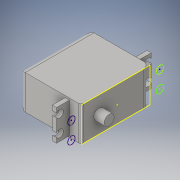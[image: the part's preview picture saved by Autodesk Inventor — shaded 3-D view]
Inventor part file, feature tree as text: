
AUTODESK INVENTOR PART (.ipt)
format: ipt  version: 2016 (Build 200138000, 138)  size: 180,224 bytes
history: native  units: in
note: dims shown in document units (in); Inventor stores cm internally (conversion verified against a paired STEP export)
features: sketch x9, extrude x6, fillet x3
ambient origin geometry x8: Origin, YZ Plane, XZ Plane, XY Plane, X Axis, Y Axis, Z Axis, Center Point
bodies: Solid1 (feature_tree)
feature tree (18):
  extrude  "Extrusion1"  Depth=0.79in
  sketch  "Sketch2"  dims[d2=1.413in d3=0.0in d4=0.389in]
  extrude  "Extrusion2"  Depth=1.413in
  extrude  "Extrusion3"  Depth=0.237in TaperAngle=0.0deg
  sketch  "Sketch5"  dims[d15=0.298in d16=0.0in d17=0.171in]
  sketch  "Sketch6"  dims[d18=0.171in d20=0.16in]
  extrude  "Extrusion4"  Depth=1.049in
  fillet  "Fillet1"  Radius=1.413in
  fillet  "Fillet2"  Radius=0.038in
  fillet  "Fillet3"  Radius=0.038in
  sketch  "Sketch9"  dims[d25=0.268in d26=0.038in d27=1.049in d28=0.038in d30=0.0in d31=0.298in d32=0.171in d33=0.16in d34=0.171in d35=0.16in d37=0.0in d38=0.096in d39=1.413in d40=0.125in d41=0.0625in d42=0.15in]
  sketch  "Sketch1"  dims[d0=1.585in d1=0.79in]
  sketch  "Sketch3"  dims[d5=0.409in d6=0.237in d7=0.0in]
  sketch  "Sketch4"  dims[d8=0.268in d9=1.049in d12=1.413in d13=0.038in d14=0.038in]
  extrude  "Extrusion5"  Depth=0.298in
  extrude  "Extrusion6"  Depth=0.16in
  sketch  "Sketch7"  dims[d22=0.16in]
  sketch  "Sketch8"  dims[d23=0.096in d24=0.0in]
